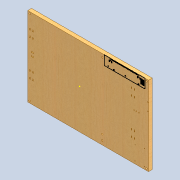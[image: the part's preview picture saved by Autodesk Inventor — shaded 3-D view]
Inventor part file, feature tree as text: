
AUTODESK INVENTOR PART (.ipt)
format: ipt  version: 2020 (Build 240168000, 168)  size: 333,312 bytes
history: native  units: mm
features: sketch x8, hole x6, other x4, extrude x3, reference x2, direct_edit x1, pattern_linear x1, projected_geometry x1, move_body x1
ambient origin geometry x8: Origin, YZ Plane, XZ Plane, XY Plane, X Axis, Y Axis, Z Axis, Center Point
bodies: Solid1 (feature_tree)
feature tree (27):
  extrude  "Extrusion1"  Depth=420.0mm
  extrude  "Extrusion2"  Depth=4.5mm
  extrude  "Extrusion3"  Depth=10.0mm
  direct_edit  "Direct Edit2"
  pattern_linear  "Rectangular Pattern1"  Count1=18  [1 undecoded]
  hole  "Hole1"  [1 undecoded]
  hole  "Hole2"  [1 undecoded]
  hole  "Hole3"  [1 undecoded]
  hole  "Hole4"  [1 undecoded]
  hole  "Hole5"  [1 undecoded]
  hole  "Hole6"  [1 undecoded]
  sketch  "Sketch1"  dims[d0=730.0mm d1=420.0mm]
  sketch  "Sketch2"  dims[d2=20.0mm d3=0.0mm d5=4.5mm]
  sketch  "Sketch3"  dims[d6=10.0mm d7=115.0mm d9=180.0mm]
  projected_geometry  "Projected Loop1"
  sketch  "Sketch5"  dims[d10=20.0mm d12=20.0mm d13=10.0mm d15=10.0mm d17=10.0mm d18=0.0mm]
  sketch  "Sketch6"  dims[d23=35.0mm d24=16.0mm]
  sketch  "Sketch7"  dims[d25=5.0mm d26=4.5mm]
  reference  "Reference3"
  reference  "Reference4"
  sketch  "Sketch8"  dims[d29=115.0mm d30=73.773mm]
  sketch  "Sketch9"  dims[d33=10.0mm d34=0.0mm d35=20.0mm d37=190.0mm d38=20.0mm d40=538.034mm d43=8.0mm d44=6.0mm d45=4.0mm d46=2.0mm d47=90.0deg d48=8.0mm d49=20.594885mm d53=0.0mm d54=0.0mm d55=-90.0mm d56=10.0mm d57=10.0mm d58=10.0mm d59=10.0mm d60=4.0mm d61=6.0mm d62=4.0mm d63=2.0mm d64=90.0deg d65=8.0mm d66=20.594885mm d67=20.0mm d68=20.0mm d69=8.0mm d70=6.0mm d71=4.0mm d72=2.0mm d73=90.0deg d74=8.0mm d75=20.594885mm d76=241.1mm d77=245.0mm d78=38.91mm d79=50.0mm d80=12.5mm d81=12.5mm d82=51.5mm d83=4.5mm d84=10.0mm d85=4.0mm d86=2.0mm d87=90.0deg d88=8.0mm d89=20.594885mm d90=2.459mm d91=20.0mm d92=4.0mm d93=2.0mm d94=90.0deg d95=8.0mm d96=20.594885mm d97=4.0mm d98=20.0mm d99=4.0mm d100=2.0mm d101=90.0deg d102=8.0mm d103=20.594885mm]
  move_body  "Move2"
  parser-record x1  (decoder bookkeeping rows leaked as tree rows — omitted from the tree; the rows remain in map.json)
  other  "0005-10-03 Y axis.iam"
  other  "0005-10-020 suport motor y.ipt:13"
  other  "0005-10-1001 NEMA17 - Motor de passo.ipt:8"
note: 7 required parameter values undecoded (feature->parameter linkage not recoverable at this tier; creation-order binding heuristic only, values carry confidence <= 0.55)
note: 1 file-system path scrubbed to <path> (originals preserved in map.json)
